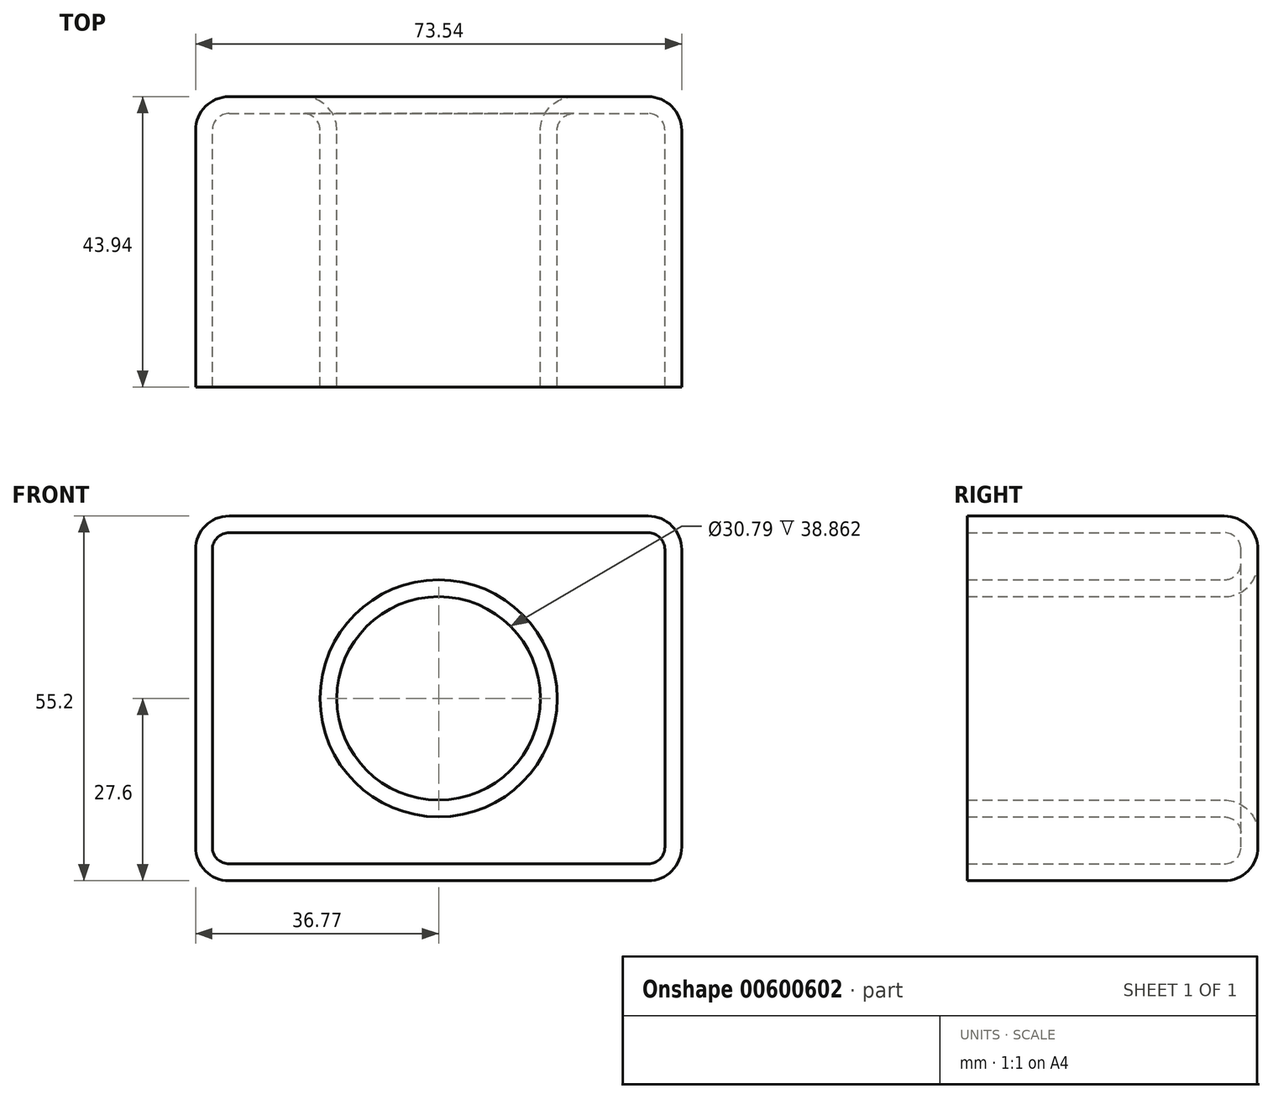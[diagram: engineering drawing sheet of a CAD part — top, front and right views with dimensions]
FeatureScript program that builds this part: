
annotation { "Feature Type Name" : "Feature", "Feature Type Description" : "" }
export const myFeature = defineFeature(function(context is Context, id is Id, definition is map)
    precondition{}
    {
        {
            var Q0;
            Q0=qCreatedBy(makeId("Front.planeOp"),FACE);
            var sketch = newSketch(context, id + "F0", { "sketchPlane" : qUnion([Q0])});
            skLineSegment(sketch, "E0.bottom", {"start": v(36.77, 27.6) * mm, "end": v(-36.77, 27.6) * mm});
            skLineSegment(sketch, "E0.top", {"start": v(36.77, -27.6) * mm, "end": v(-36.77, -27.6) * mm});
            skLineSegment(sketch, "E0.left", {"start": v(36.77, 27.6) * mm, "end": v(36.77, -27.6) * mm});
            skLineSegment(sketch, "E0.right", {"start": v(-36.77, 27.6) * mm, "end": v(-36.77, -27.6) * mm});
            skPoint(sketch, "E0.middle", {"position": v(0, 0) * mm});
            skCircle(sketch, "E1", {"center": v(0, 0) * mm, "radius": 15.4 * mm});
            skSolve(sketch);
        }
        {
            var Q0;
            Q0 = qSketchRegion(id + "F0", true);
            extrude(context, id + "F1", {"entities" : qUnion([Q0]), "depth" : 43.94 * mm, "offsetDistance" : 25.4 * mm});
        }
        {
            var Q0;
            Q0=makeQuery(id+"F1.opExtrude","CAP_FACE",FACE,{"disambiguationData":[OSD([sQuery(id+"F0.wireOp",EDGE,"E0.bottom"),sQuery(id+"F0.wireOp",EDGE,"E0.top"),sQuery(id+"F0.wireOp",EDGE,"E0.left"),sQuery(id+"F0.wireOp",EDGE,"E0.right"),sQuery(id+"F0.wireOp",EDGE,"E1")])],"isStart":true});
            var Q1;
            Q1=makeQuery(id+"F1.opExtrude","SWEPT_EDGE",EDGE,{"disambiguationData":[OSD([sQuery(id+"F0.wireOp",EDGE,"E0.top"),sQuery(id+"F0.wireOp",EDGE,"E0.right")])]});
            var Q2;
            Q2=makeQuery(id+"F1.opExtrude","SWEPT_EDGE",EDGE,{"disambiguationData":[OSD([sQuery(id+"F0.wireOp",EDGE,"E0.top"),sQuery(id+"F0.wireOp",EDGE,"E0.left")])]});
            var Q3;
            Q3=makeQuery(id+"F1.opExtrude","SWEPT_EDGE",EDGE,{"disambiguationData":[OSD([sQuery(id+"F0.wireOp",EDGE,"E0.bottom"),sQuery(id+"F0.wireOp",EDGE,"E0.left")])]});
            var Q4;
            Q4=makeQuery(id+"F1.opExtrude","SWEPT_EDGE",EDGE,{"disambiguationData":[OSD([sQuery(id+"F0.wireOp",EDGE,"E0.bottom"),sQuery(id+"F0.wireOp",EDGE,"E0.right")])]});
            fillet(context, id + "F2", {"entities" : qUnion([Q0, Q1, Q2, Q3, Q4]), "radius" : 5.08 * mm, "tangentPropagation" : true, "allowEdgeOverflow" : false});
        }
        {
            var Q0;
            Q0=makeQuery(id+"F1.opExtrude","CAP_FACE",FACE,{"disambiguationData":[OSD([sQuery(id+"F0.wireOp",EDGE,"E0.bottom"),sQuery(id+"F0.wireOp",EDGE,"E0.top"),sQuery(id+"F0.wireOp",EDGE,"E0.left"),sQuery(id+"F0.wireOp",EDGE,"E0.right"),sQuery(id+"F0.wireOp",EDGE,"E1")])],"isStart":false});
            shell(context, id + "F3", {"entities" : qUnion([Q0]), "thickness" : 2.54 * mm});
        }
    });
